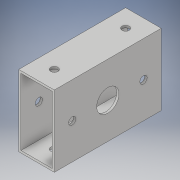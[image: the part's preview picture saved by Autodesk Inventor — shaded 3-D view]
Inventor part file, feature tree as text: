
AUTODESK INVENTOR PART (.ipt)
format: ipt  version: 2018 (Build 220112000, 112)  size: 140,800 bytes
history: native  units: in
note: dims shown in document units (in); Inventor stores cm internally (conversion verified against a paired STEP export)
features: extrude x5, sketch x5
ambient origin geometry x8: Origin, YZ Plane, XZ Plane, XY Plane, X Axis, Y Axis, Z Axis, Center Point
bodies: Solid1 (feature_tree)
feature tree (10):
  extrude  "Extrusion1"  Depth=2.0in
  extrude  "Extrusion2"  Depth=3.0in TaperAngle=0.0deg
  extrude  "Extrusion3"  Depth=0.1875in TaperAngle=0.0deg
  extrude  "Extrusion4"  Depth=0.1875in TaperAngle=0.0deg
  extrude  "Extrusion5"  Depth=2.0in
  sketch  "Sketch1"  dims[d0=1.0in d1=2.0in]
  sketch  "Sketch2"  dims[d2=0.0625in d3=3.0in d4=0.0in]
  sketch  "Sketch3"  dims[d5=0.625in d6=0.1875in d7=0.0in]
  sketch  "Sketch4"  dims[d8=0.5in d9=0.1875in d10=0.0in]
  sketch  "Sketch5"  dims[d11=0.5in d12=2.0in d13=0.2031in d14=2.1875in d15=0.0in d16=0.5in d17=2.0in d18=0.2031in d19=2.625in d20=0.0in]
